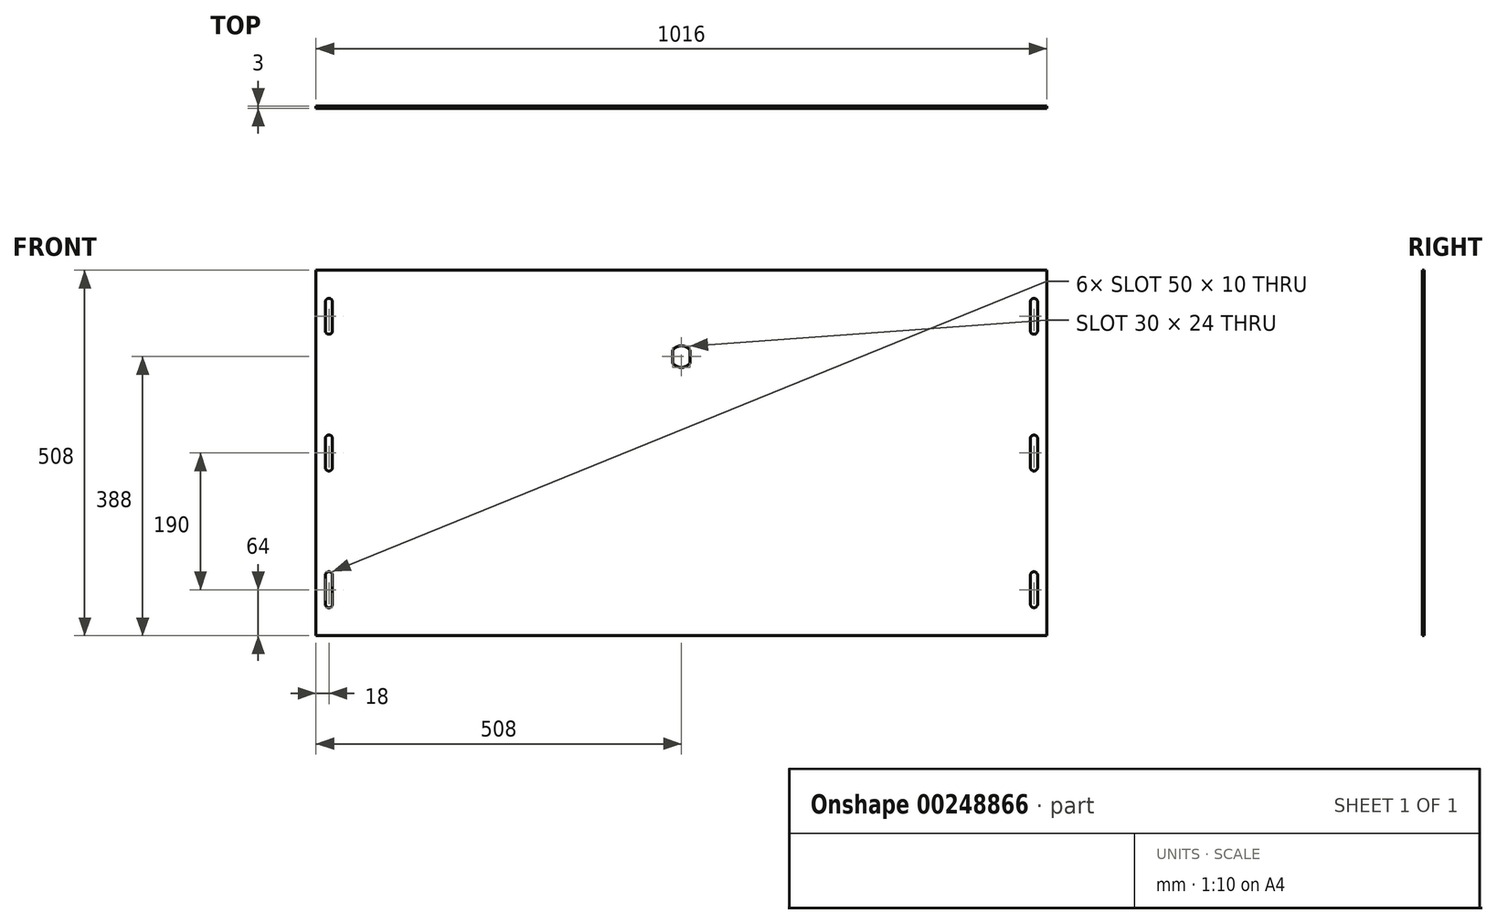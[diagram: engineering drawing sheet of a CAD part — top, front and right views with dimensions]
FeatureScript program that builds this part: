
annotation { "Feature Type Name" : "Feature", "Feature Type Description" : "" }
export const myFeature = defineFeature(function(context is Context, id is Id, definition is map)
    precondition{}
    {
        {
            var Q0;
            Q0=qCreatedBy(makeId("Front.planeOp"),FACE);
            var sketch = newSketch(context, id + "F0", { "sketchPlane" : qUnion([Q0])});
            skLineSegment(sketch, "E0.bottom", {"start": v(0, 0) * mm, "end": v(1016, 0) * mm});
            skLineSegment(sketch, "E0.top", {"start": v(0, 508) * mm, "end": v(1016, 508) * mm});
            skLineSegment(sketch, "E0.left", {"start": v(0, 0) * mm, "end": v(0, 508) * mm});
            skLineSegment(sketch, "E0.right", {"start": v(1016, 0) * mm, "end": v(1016, 508) * mm});
            skLineSegment(sketch, "E1", {"start": v(18, 508) * mm, "end": v(18, 0) * mm, "construction": true});
            skLineSegment(sketch, "E2", {"start": v(998, 508) * mm, "end": v(998, 0) * mm, "construction": true});
            skArc(sketch, "E3", {"start": v(23, 464) * mm, "mid": v(18, 469) * mm, "end": v(13, 464) * mm});
            skArc(sketch, "E4", {"start": v(13, 424) * mm, "mid": v(18, 419) * mm, "end": v(23, 424) * mm});
            skArc(sketch, "E5", {"start": v(23, 274) * mm, "mid": v(18, 279) * mm, "end": v(13, 274) * mm});
            skArc(sketch, "E6", {"start": v(13, 234) * mm, "mid": v(18, 229) * mm, "end": v(23, 234) * mm});
            skArc(sketch, "E7", {"start": v(23, 84) * mm, "mid": v(18, 89) * mm, "end": v(13, 84) * mm});
            skArc(sketch, "E8", {"start": v(13, 44) * mm, "mid": v(18, 39) * mm, "end": v(23, 44) * mm});
            skLineSegment(sketch, "E9", {"start": v(13, 464) * mm, "end": v(13, 424) * mm});
            skLineSegment(sketch, "E10", {"start": v(23, 464) * mm, "end": v(23, 424) * mm});
            skLineSegment(sketch, "E11", {"start": v(13, 274) * mm, "end": v(13, 234) * mm});
            skLineSegment(sketch, "E12", {"start": v(23, 274) * mm, "end": v(23, 234) * mm});
            skLineSegment(sketch, "E13", {"start": v(13, 84) * mm, "end": v(13, 44) * mm});
            skLineSegment(sketch, "E14", {"start": v(23, 84) * mm, "end": v(23, 44) * mm});
            skArc(sketch, "E15", {"start": v(1003, 464) * mm, "mid": v(998, 469) * mm, "end": v(993, 464) * mm});
            skArc(sketch, "E16", {"start": v(993, 424) * mm, "mid": v(998, 419) * mm, "end": v(1003, 424) * mm});
            skArc(sketch, "E17", {"start": v(1003, 274) * mm, "mid": v(998, 279) * mm, "end": v(993, 274) * mm});
            skArc(sketch, "E18", {"start": v(993, 234) * mm, "mid": v(998, 229) * mm, "end": v(1003, 234) * mm});
            skArc(sketch, "E19", {"start": v(993, 44) * mm, "mid": v(998, 39) * mm, "end": v(1003, 44) * mm});
            skArc(sketch, "E20", {"start": v(1003, 84) * mm, "mid": v(998, 89) * mm, "end": v(993, 84) * mm});
            skLineSegment(sketch, "E21", {"start": v(993, 464) * mm, "end": v(993, 424) * mm});
            skLineSegment(sketch, "E22", {"start": v(1003, 464) * mm, "end": v(1003, 424) * mm});
            skLineSegment(sketch, "E23", {"start": v(993, 274) * mm, "end": v(993, 234) * mm});
            skLineSegment(sketch, "E24", {"start": v(1003, 274) * mm, "end": v(1003, 234) * mm});
            skLineSegment(sketch, "E25", {"start": v(993, 84) * mm, "end": v(993, 44) * mm});
            skLineSegment(sketch, "E26", {"start": v(1003, 84) * mm, "end": v(1003, 44) * mm});
            skLineSegment(sketch, "E27", {"start": v(508, 508) * mm, "end": v(508, 388) * mm, "construction": true});
            skArc(sketch, "E28", {"start": v(496, 379) * mm, "mid": v(508, 373) * mm, "end": v(520, 379) * mm});
            skLineSegment(sketch, "E29", {"start": v(496, 397) * mm, "end": v(496, 379) * mm});
            skLineSegment(sketch, "E30", {"start": v(520, 397) * mm, "end": v(520, 379) * mm});
            skArc(sketch, "E31.trimOffspring", {"start": v(520, 397) * mm, "mid": v(508, 403) * mm, "end": v(496, 397) * mm});
            skSolve(sketch);
        }
        {
            var Q0;
            Q0=qSketchRegion(id+"F0",true);
            extrude(context, id + "F1", {"entities" : qUnion([Q0]), "depth" : 3 * mm});
        }
    });
